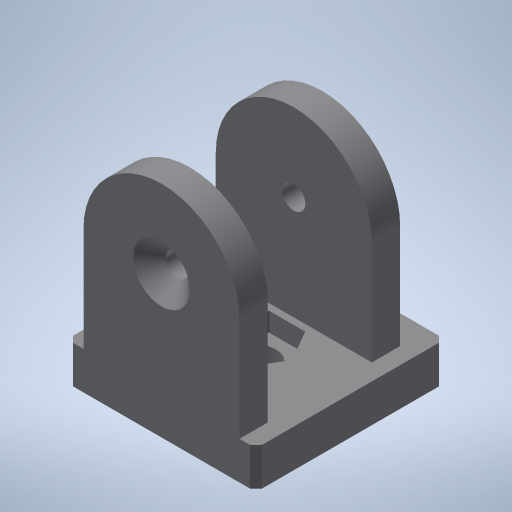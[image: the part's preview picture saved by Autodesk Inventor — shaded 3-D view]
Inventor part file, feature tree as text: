
AUTODESK INVENTOR PART (.ipt)
format: ipt  version: 2023 (Build 270158000, 158)  size: 326,144 bytes
history: native  units: mm
features: other x70, sketch x10, extrude x8, hole x2, chamfer x1
ambient origin geometry x8: Origin, YZ Plane, XZ Plane, XY Plane, X Axis, Y Axis, Z Axis, Center Point
bodies: Solid1 (feature_tree)
feature tree (91):
  extrude  "Extrusion1"  Depth=42.0mm TaperAngle=0.0deg
  extrude  "Extrusion2"  Depth=6.5mm TaperAngle=0.0deg
  extrude  "Extrusion3"  Depth=6.5mm TaperAngle=0.0deg
  hole  "Hole1"  [1 undecoded]
  extrude  "Extrusion4"  TaperAngle=0.0deg  [1 undecoded]
  extrude  "Extrusion5"  TaperAngle=0.0deg  [1 undecoded]
  extrude  "Extrusion6"  TaperAngle=0.0deg  [1 undecoded]
  extrude  "Extrusion7"  TaperAngle=0.0deg  [1 undecoded]
  hole  "Hole2"  [1 undecoded]
  extrude  "Extrusion8"  [1 undecoded]
  other  "GN300Klemmhebel_XY"
  other  "GN300Klemmhebel_YZ"
  other  "GN300Klemmhebel_ZX"
  other  "GN300Klemmhebel_X"
  other  "GN300Klemmhebel_Y"
  other  "GN300Klemmhebel_Z"
  other  "GN300Klemmhebel_Center"
  other  "GUS_4_41_XY"
  other  "GUS_4_41_YZ"
  other  "GUS_4_41_ZX"
  other  "GUS_4_41_X"
  other  "GUS_4_41_Y"
  other  "GUS_4_41_Z"
  other  "GUS_4_41_Center"
  other  "GUS_4_41_L_XY"
  other  "GUS_4_41_L_YZ"
  other  "GUS_4_41_L_ZX"
  other  "GUS_4_41_L_X"
  other  "GUS_4_41_L_Y"
  other  "GUS_4_41_L_Z"
  other  "GUS_4_41_L_Center"
  other  "GUS_4_41_R_XY"
  other  "GUS_4_41_R_YZ"
  other  "GUS_4_41_R_ZX"
  other  "GUS_4_41_R_X"
  other  "GUS_4_41_R_Y"
  other  "GUS_4_41_R_Z"
  other  "GUS_4_41_R_Center"
  other  "p0_XY"
  other  "p0_YZ"
  other  "p0_ZX"
  other  "p0_X"
  other  "p0_Y"
  other  "p0_Z"
  other  "p0_Center"
  other  "p1_XY"
  other  "p1_YZ"
  other  "p1_ZX"
  other  "p1_X"
  other  "p1_Y"
  other  "p1_Z"
  other  "p1_Center"
  other  "p2_XY"
  other  "p2_YZ"
  other  "p2_ZX"
  other  "p2_X"
  other  "p2_Y"
  other  "p2_Z"
  other  "p2_Center"
  other  "p3_XY"
  other  "p3_YZ"
  other  "p3_ZX"
  other  "p3_X"
  other  "p3_Y"
  other  "p3_Z"
  other  "p3_Center"
  other  "p4_XY"
  other  "p4_YZ"
  other  "p4_ZX"
  other  "p4_X"
  other  "p4_Y"
  other  "p4_Z"
  other  "p4_Center"
  other  "ps_XY"
  other  "ps_YZ"
  other  "ps_ZX"
  other  "ps_X"
  other  "ps_Y"
  other  "ps_Z"
  other  "ps_Center"
  chamfer  "Chamfer1"  [1 undecoded]
  sketch  "Skizze_1"  dims[d0=52.0mm d1=0.0mm d2=42.0mm d3=0.0mm]
  sketch  "Skizze_2"  dims[d6=4.92mm d7=6.0mm d8=12.0mm d9=2.0mm d10=16.40943mm d11=39.8mm d12=0.0mm d13=6.5mm d14=0.0mm]
  sketch  "Skizze_3"  dims[d19=6.5mm d20=0.0mm]
  sketch  "Sketch4"  dims[d30=0.0mm d31=0.0mm]
  sketch  "Sketch_1"  dims[d4=42.0mm d5=0.0mm]
  sketch  "Sketch_2"  dims[d15=6.5mm d16=0.0mm d17=6.5mm d18=0.0mm]
  sketch  "Sketch_3"  dims[d21=8.5mm d22=6.0mm d23=4.0mm d24=2.0mm d25=90.0deg d26=8.0mm d27=0.0mm d28=4.0mm d29=0.0mm]
  sketch  "Sketch_4"  dims[d32=0.0mm d33=0.0mm]
  sketch  "Sketch9"  dims[d36=0.0mm d37=0.0mm d38=1.25mm d39=2.0mm d40=45.0deg]
  sketch  "Sketch_5"  dims[d34=0.0mm d35=0.0mm]
note: 8 required parameter values undecoded (feature->parameter linkage not recoverable at this tier; creation-order binding heuristic only, values carry confidence <= 0.55)
